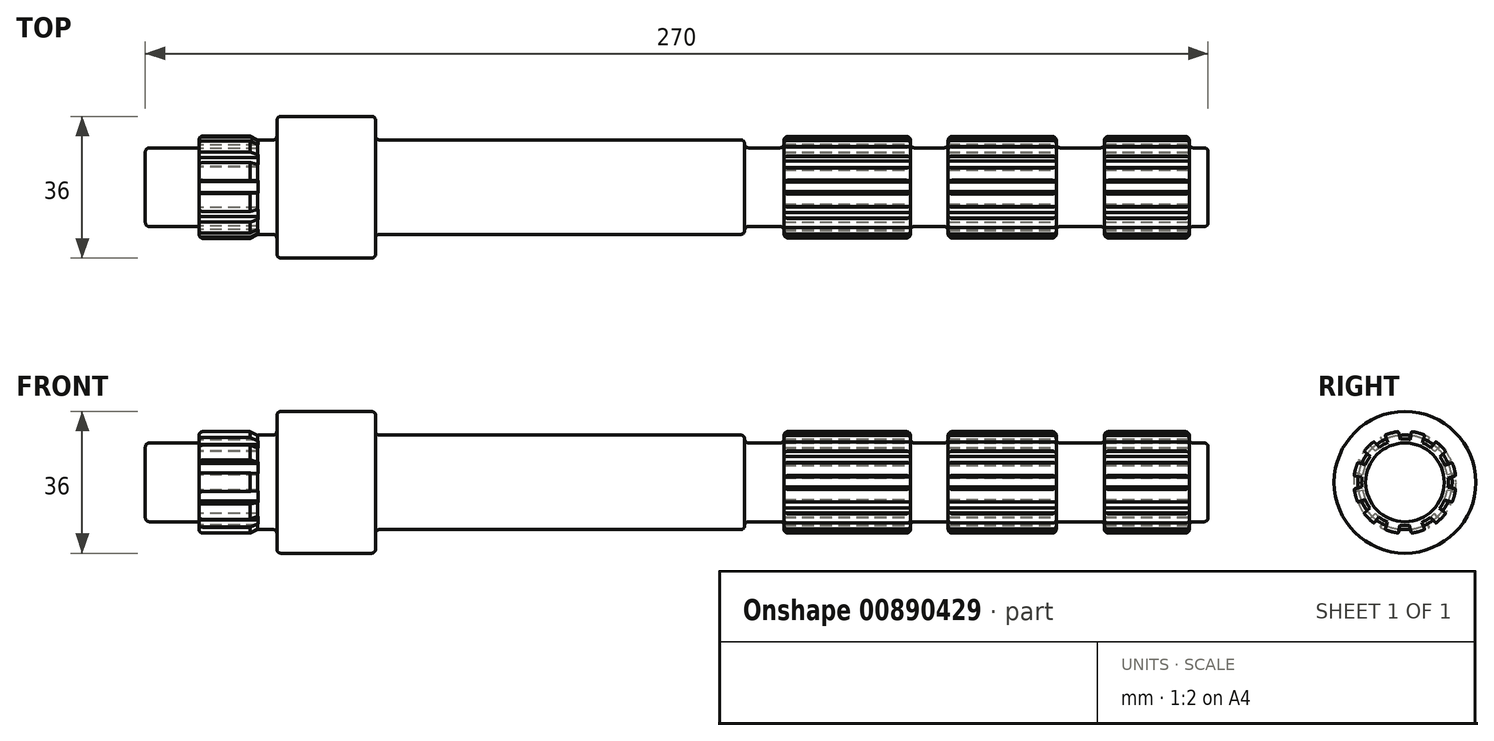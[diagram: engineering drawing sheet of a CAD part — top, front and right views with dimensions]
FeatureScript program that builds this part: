
annotation { "Feature Type Name" : "Feature", "Feature Type Description" : "" }
export const myFeature = defineFeature(function(context is Context, id is Id, definition is map)
    precondition{}
    {
        {
            var Q0;
            Q0=qCreatedBy(makeId("Front.planeOp"),FACE);
            var sketch = newSketch(context, id + "F0", { "sketchPlane" : qUnion([Q0])});
            skLineSegment(sketch, "E0", {"start": v(0, 0) * mm, "end": v(0, 9) * mm});
            skLineSegment(sketch, "E1", {"start": v(1, 10) * mm, "end": v(13.63, 10) * mm});
            skLineSegment(sketch, "E2", {"start": v(13.63, 10) * mm, "end": v(13.63, 12) * mm});
            skLineSegment(sketch, "E3", {"start": v(14.63, 13) * mm, "end": v(26.57, 13) * mm});
            skLineSegment(sketch, "E4", {"start": v(28.57, 12) * mm, "end": v(32.41, 12) * mm});
            skLineSegment(sketch, "E5", {"start": v(33.41, 13) * mm, "end": v(33.41, 17) * mm});
            skLineSegment(sketch, "E6", {"start": v(34.41, 18) * mm, "end": v(57.48, 18) * mm});
            skLineSegment(sketch, "E7", {"start": v(58.48, 17) * mm, "end": v(58.48, 13) * mm});
            skLineSegment(sketch, "E8", {"start": v(59.48, 12) * mm, "end": v(151.25, 12) * mm});
            skLineSegment(sketch, "E9", {"start": v(152.25, 11) * mm, "end": v(152.25, 11) * mm});
            skLineSegment(sketch, "E10", {"start": v(153.25, 10) * mm, "end": v(161.25, 10) * mm});
            skLineSegment(sketch, "E11", {"start": v(162.25, 11) * mm, "end": v(162.25, 12) * mm});
            skLineSegment(sketch, "E12", {"start": v(163.25, 13) * mm, "end": v(193.36, 13) * mm});
            skLineSegment(sketch, "E13", {"start": v(194.36, 12) * mm, "end": v(194.36, 11) * mm});
            skLineSegment(sketch, "E14", {"start": v(195.36, 10) * mm, "end": v(202.96, 10) * mm});
            skLineSegment(sketch, "E15", {"start": v(203.96, 11) * mm, "end": v(203.96, 12) * mm});
            skLineSegment(sketch, "E16", {"start": v(204.96, 13) * mm, "end": v(230.4, 13) * mm});
            skLineSegment(sketch, "E17", {"start": v(231.4, 12) * mm, "end": v(231.4, 11) * mm});
            skLineSegment(sketch, "E18", {"start": v(232.4, 10) * mm, "end": v(242.67, 10) * mm});
            skLineSegment(sketch, "E19", {"start": v(243.67, 11) * mm, "end": v(243.67, 12) * mm});
            skLineSegment(sketch, "E20", {"start": v(244.67, 13) * mm, "end": v(264.2, 13) * mm});
            skLineSegment(sketch, "E21", {"start": v(265.2, 12) * mm, "end": v(265.2, 11) * mm});
            skLineSegment(sketch, "E22", {"start": v(266.2, 10) * mm, "end": v(269, 10) * mm});
            skLineSegment(sketch, "E23", {"start": v(270, 9) * mm, "end": v(270, 0) * mm});
            skLineSegment(sketch, "E24", {"start": v(270, 0) * mm, "end": v(0, 0) * mm});
            skPoint(sketch, "E25.visualSharp", {"position": v(0, 10) * mm});
            skArc(sketch, "E25.filletArc", {"start": v(1, 10) * mm, "mid": v(0.3, 9.7) * mm, "end": v(0, 9) * mm});
            skPoint(sketch, "E26.visualSharp", {"position": v(13.63, 13) * mm});
            skArc(sketch, "E26.filletArc", {"start": v(14.63, 13) * mm, "mid": v(13.92, 12.7) * mm, "end": v(13.63, 12) * mm});
            skPoint(sketch, "E27.visualSharp", {"position": v(33.41, 12) * mm});
            skArc(sketch, "E27.filletArc", {"start": v(32.41, 12) * mm, "mid": v(33.12, 12.3) * mm, "end": v(33.41, 13) * mm});
            skPoint(sketch, "E28.visualSharp", {"position": v(33.41, 18) * mm});
            skArc(sketch, "E28.filletArc", {"start": v(34.41, 18) * mm, "mid": v(33.7, 17.7) * mm, "end": v(33.41, 17) * mm});
            skPoint(sketch, "E29.visualSharp", {"position": v(58.48, 18) * mm});
            skArc(sketch, "E29.filletArc", {"start": v(58.48, 17) * mm, "mid": v(58.19, 17.7) * mm, "end": v(57.48, 18) * mm});
            skPoint(sketch, "E30.visualSharp", {"position": v(58.48, 12) * mm});
            skArc(sketch, "E30.filletArc", {"start": v(58.48, 13) * mm, "mid": v(58.77, 12.3) * mm, "end": v(59.48, 12) * mm});
            skPoint(sketch, "E31.visualSharp", {"position": v(152.25, 12) * mm});
            skArc(sketch, "E31.filletArc", {"start": v(152.25, 11) * mm, "mid": v(151.96, 11.7) * mm, "end": v(151.25, 12) * mm});
            skPoint(sketch, "E32.visualSharp", {"position": v(152.25, 10) * mm});
            skArc(sketch, "E32.filletArc", {"start": v(152.25, 11) * mm, "mid": v(152.55, 10.3) * mm, "end": v(153.25, 10) * mm});
            skPoint(sketch, "E33.visualSharp", {"position": v(162.25, 10) * mm});
            skArc(sketch, "E33.filletArc", {"start": v(161.25, 10) * mm, "mid": v(161.96, 10.3) * mm, "end": v(162.25, 11) * mm});
            skPoint(sketch, "E34.visualSharp", {"position": v(162.25, 13) * mm});
            skArc(sketch, "E34.filletArc", {"start": v(163.25, 13) * mm, "mid": v(162.55, 12.7) * mm, "end": v(162.25, 12) * mm});
            skPoint(sketch, "E35.visualSharp", {"position": v(194.36, 13) * mm});
            skArc(sketch, "E35.filletArc", {"start": v(194.36, 12) * mm, "mid": v(194.07, 12.7) * mm, "end": v(193.36, 13) * mm});
            skPoint(sketch, "E36.visualSharp", {"position": v(194.36, 10) * mm});
            skArc(sketch, "E36.filletArc", {"start": v(194.36, 11) * mm, "mid": v(194.66, 10.3) * mm, "end": v(195.36, 10) * mm});
            skPoint(sketch, "E37.visualSharp", {"position": v(203.96, 10) * mm});
            skArc(sketch, "E37.filletArc", {"start": v(202.96, 10) * mm, "mid": v(203.66, 10.3) * mm, "end": v(203.96, 11) * mm});
            skPoint(sketch, "E38.visualSharp", {"position": v(203.96, 13) * mm});
            skArc(sketch, "E38.filletArc", {"start": v(204.96, 13) * mm, "mid": v(204.25, 12.7) * mm, "end": v(203.96, 12) * mm});
            skPoint(sketch, "E39.visualSharp", {"position": v(231.4, 13) * mm});
            skArc(sketch, "E39.filletArc", {"start": v(231.4, 12) * mm, "mid": v(231.12, 12.7) * mm, "end": v(230.4, 13) * mm});
            skPoint(sketch, "E40.visualSharp", {"position": v(231.4, 10) * mm});
            skArc(sketch, "E40.filletArc", {"start": v(231.4, 11) * mm, "mid": v(231.7, 10.3) * mm, "end": v(232.4, 10) * mm});
            skPoint(sketch, "E41.visualSharp", {"position": v(243.67, 10) * mm});
            skArc(sketch, "E41.filletArc", {"start": v(242.67, 10) * mm, "mid": v(243.38, 10.3) * mm, "end": v(243.67, 11) * mm});
            skPoint(sketch, "E42.visualSharp", {"position": v(243.67, 13) * mm});
            skArc(sketch, "E42.filletArc", {"start": v(244.67, 13) * mm, "mid": v(243.96, 12.7) * mm, "end": v(243.67, 12) * mm});
            skPoint(sketch, "E43.visualSharp", {"position": v(265.2, 13) * mm});
            skArc(sketch, "E43.filletArc", {"start": v(265.2, 12) * mm, "mid": v(264.9, 12.7) * mm, "end": v(264.2, 13) * mm});
            skPoint(sketch, "E44.visualSharp", {"position": v(265.2, 10) * mm});
            skArc(sketch, "E44.filletArc", {"start": v(265.2, 11) * mm, "mid": v(265.5, 10.3) * mm, "end": v(266.2, 10) * mm});
            skPoint(sketch, "E45.visualSharp", {"position": v(270, 10) * mm});
            skArc(sketch, "E45.filletArc", {"start": v(270, 9) * mm, "mid": v(269.7, 9.7) * mm, "end": v(269, 10) * mm});
            skLineSegment(sketch, "E46", {"start": v(26.57, 13) * mm, "end": v(28.57, 12) * mm});
            skSolve(sketch);
        }
        {
            var Q0;
            Q0 = qSketchRegion(id + "F0", true);
            var Q1;
            Q1=sQuery(id+"F0.wireOp",EDGE,"E24");
            revolve(context, id + "F1", {"surfaceOperationType" : NewSurfaceOperationType.NEW, "entities" : qUnion([Q0]), "axis" : qUnion([Q1]), "revolveType" : RevolveType.FULL});
        }
        {
            var Q0;
            Q0=makeQuery(id+"F1.opRevolve","SWEPT_FACE",FACE,{"disambiguationData":[OSD([sQuery(id+"F0.wireOp",EDGE,"E2")])]});
            var sketch = newSketch(context, id + "F2", { "sketchPlane" : qUnion([Q0])});
            skLineSegment(sketch, "E47", {"start": v(-1.55, 13.03) * mm, "end": v(1.45, 13.03) * mm});
            skPoint(sketch, "E48.visualSharp", {"position": v(-1.75, 13.03) * mm});
            skArc(sketch, "E48.filletArc", {"start": v(-1.55, 13.03) * mm, "mid": v(-1.7, 12.97) * mm, "end": v(-1.75, 12.83) * mm});
            skPoint(sketch, "E49.visualSharp", {"position": v(1.65, 13.03) * mm});
            skArc(sketch, "E49.filletArc", {"start": v(1.65, 12.83) * mm, "mid": v(1.6, 12.97) * mm, "end": v(1.45, 13.03) * mm});
            skLineSegment(sketch, "E50", {"start": v(-1.75, 12.83) * mm, "end": v(-1.47, 10.8) * mm});
            skLineSegment(sketch, "E51", {"start": v(1.65, 12.83) * mm, "end": v(1.4, 10.82) * mm});
            skLineSegment(sketch, "E52.1.0", {"start": v(-8.91, 9.63) * mm, "end": v(-6.49, 11.4) * mm});
            skLineSegment(sketch, "E52.1.1", {"start": v(-8.96, 9.35) * mm, "end": v(-7.54, 7.88) * mm});
            skLineSegment(sketch, "E52.1.2", {"start": v(-6.2, 11.35) * mm, "end": v(-5.23, 9.57) * mm});
            skPoint(sketch, "E52.1.3", {"position": v(-6.33, 11.51) * mm});
            skPoint(sketch, "E52.1.4", {"position": v(-9.08, 9.52) * mm});
            skArc(sketch, "E52.1.5", {"start": v(-8.91, 9.63) * mm, "mid": v(-9, 9.5) * mm, "end": v(-8.96, 9.35) * mm});
            skArc(sketch, "E52.1.6", {"start": v(-6.2, 11.35) * mm, "mid": v(-6.34, 11.43) * mm, "end": v(-6.49, 11.4) * mm});
            skLineSegment(sketch, "E52.2.0", {"start": v(-12.87, 2.55) * mm, "end": v(-11.95, 5.4) * mm});
            skLineSegment(sketch, "E52.2.1", {"start": v(-12.75, 2.3) * mm, "end": v(-10.73, 1.94) * mm});
            skLineSegment(sketch, "E52.2.2", {"start": v(-11.7, 5.53) * mm, "end": v(-9.86, 4.67) * mm});
            skPoint(sketch, "E52.2.3", {"position": v(-11.89, 5.6) * mm});
            skPoint(sketch, "E52.2.4", {"position": v(-12.94, 2.36) * mm});
            skArc(sketch, "E52.2.5", {"start": v(-12.87, 2.55) * mm, "mid": v(-12.86, 2.4) * mm, "end": v(-12.75, 2.3) * mm});
            skArc(sketch, "E52.2.6", {"start": v(-11.7, 5.53) * mm, "mid": v(-11.85, 5.52) * mm, "end": v(-11.95, 5.4) * mm});
            skLineSegment(sketch, "E52.3.0", {"start": v(-11.92, -5.5) * mm, "end": v(-12.84, -2.65) * mm});
            skLineSegment(sketch, "E52.3.1", {"start": v(-11.66, -5.63) * mm, "end": v(-9.82, -4.74) * mm});
            skLineSegment(sketch, "E52.3.2", {"start": v(-12.71, -2.4) * mm, "end": v(-10.72, -2.02) * mm});
            skPoint(sketch, "E52.3.3", {"position": v(-12.9, -2.46) * mm});
            skPoint(sketch, "E52.3.4", {"position": v(-11.85, -5.7) * mm});
            skArc(sketch, "E52.3.5", {"start": v(-11.92, -5.5) * mm, "mid": v(-11.82, -5.62) * mm, "end": v(-11.66, -5.63) * mm});
            skArc(sketch, "E52.3.6", {"start": v(-12.71, -2.4) * mm, "mid": v(-12.83, -2.5) * mm, "end": v(-12.84, -2.65) * mm});
            skLineSegment(sketch, "E52.4.0", {"start": v(-6.4, -11.45) * mm, "end": v(-8.83, -9.7) * mm});
            skLineSegment(sketch, "E52.4.1", {"start": v(-6.13, -11.41) * mm, "end": v(-5.16, -9.6) * mm});
            skLineSegment(sketch, "E52.4.2", {"start": v(-8.88, -9.41) * mm, "end": v(-7.48, -7.93) * mm});
            skPoint(sketch, "E52.4.3", {"position": v(-9, -9.57) * mm});
            skPoint(sketch, "E52.4.4", {"position": v(-6.24, -11.57) * mm});
            skArc(sketch, "E52.4.5", {"start": v(-6.4, -11.45) * mm, "mid": v(-6.26, -11.5) * mm, "end": v(-6.13, -11.41) * mm});
            skArc(sketch, "E52.4.6", {"start": v(-8.88, -9.41) * mm, "mid": v(-8.91, -9.56) * mm, "end": v(-8.83, -9.7) * mm});
            skLineSegment(sketch, "E52.5.0", {"start": v(1.55, -13.03) * mm, "end": v(-1.45, -13.03) * mm});
            skLineSegment(sketch, "E52.5.1", {"start": v(1.75, -12.83) * mm, "end": v(1.47, -10.8) * mm});
            skLineSegment(sketch, "E52.5.2", {"start": v(-1.65, -12.83) * mm, "end": v(-1.4, -10.82) * mm});
            skPoint(sketch, "E52.5.3", {"position": v(-1.65, -13.03) * mm});
            skPoint(sketch, "E52.5.4", {"position": v(1.75, -13.03) * mm});
            skArc(sketch, "E52.5.5", {"start": v(1.55, -13.03) * mm, "mid": v(1.7, -12.97) * mm, "end": v(1.75, -12.83) * mm});
            skArc(sketch, "E52.5.6", {"start": v(-1.65, -12.83) * mm, "mid": v(-1.6, -12.97) * mm, "end": v(-1.45, -13.03) * mm});
            skLineSegment(sketch, "E52.6.0", {"start": v(8.91, -9.63) * mm, "end": v(6.49, -11.4) * mm});
            skLineSegment(sketch, "E52.6.1", {"start": v(8.96, -9.35) * mm, "end": v(7.54, -7.88) * mm});
            skLineSegment(sketch, "E52.6.2", {"start": v(6.2, -11.35) * mm, "end": v(5.23, -9.57) * mm});
            skPoint(sketch, "E52.6.3", {"position": v(6.33, -11.51) * mm});
            skPoint(sketch, "E52.6.4", {"position": v(9.08, -9.52) * mm});
            skArc(sketch, "E52.6.5", {"start": v(8.91, -9.63) * mm, "mid": v(9, -9.5) * mm, "end": v(8.96, -9.35) * mm});
            skArc(sketch, "E52.6.6", {"start": v(6.2, -11.35) * mm, "mid": v(6.34, -11.43) * mm, "end": v(6.49, -11.4) * mm});
            skLineSegment(sketch, "E52.7.0", {"start": v(12.87, -2.55) * mm, "end": v(11.95, -5.4) * mm});
            skLineSegment(sketch, "E52.7.1", {"start": v(12.75, -2.3) * mm, "end": v(10.73, -1.94) * mm});
            skLineSegment(sketch, "E52.7.2", {"start": v(11.7, -5.53) * mm, "end": v(9.86, -4.67) * mm});
            skPoint(sketch, "E52.7.3", {"position": v(11.89, -5.6) * mm});
            skPoint(sketch, "E52.7.4", {"position": v(12.94, -2.36) * mm});
            skArc(sketch, "E52.7.5", {"start": v(12.87, -2.55) * mm, "mid": v(12.86, -2.4) * mm, "end": v(12.75, -2.3) * mm});
            skArc(sketch, "E52.7.6", {"start": v(11.7, -5.53) * mm, "mid": v(11.85, -5.52) * mm, "end": v(11.95, -5.4) * mm});
            skLineSegment(sketch, "E52.8.0", {"start": v(11.92, 5.5) * mm, "end": v(12.84, 2.65) * mm});
            skLineSegment(sketch, "E52.8.1", {"start": v(11.66, 5.63) * mm, "end": v(9.82, 4.74) * mm});
            skLineSegment(sketch, "E52.8.2", {"start": v(12.71, 2.4) * mm, "end": v(10.72, 2.02) * mm});
            skPoint(sketch, "E52.8.3", {"position": v(12.9, 2.46) * mm});
            skPoint(sketch, "E52.8.4", {"position": v(11.85, 5.7) * mm});
            skArc(sketch, "E52.8.5", {"start": v(11.92, 5.5) * mm, "mid": v(11.82, 5.62) * mm, "end": v(11.66, 5.63) * mm});
            skArc(sketch, "E52.8.6", {"start": v(12.71, 2.4) * mm, "mid": v(12.83, 2.5) * mm, "end": v(12.84, 2.65) * mm});
            skLineSegment(sketch, "E52.9.0", {"start": v(6.4, 11.45) * mm, "end": v(8.83, 9.7) * mm});
            skLineSegment(sketch, "E52.9.1", {"start": v(6.13, 11.41) * mm, "end": v(5.16, 9.6) * mm});
            skLineSegment(sketch, "E52.9.2", {"start": v(8.88, 9.41) * mm, "end": v(7.48, 7.93) * mm});
            skPoint(sketch, "E52.9.3", {"position": v(9, 9.57) * mm});
            skPoint(sketch, "E52.9.4", {"position": v(6.24, 11.57) * mm});
            skArc(sketch, "E52.9.5", {"start": v(6.4, 11.45) * mm, "mid": v(6.26, 11.5) * mm, "end": v(6.13, 11.41) * mm});
            skArc(sketch, "E52.9.6", {"start": v(8.88, 9.41) * mm, "mid": v(8.91, 9.56) * mm, "end": v(8.83, 9.7) * mm});
            skPoint(sketch, "E52.center", {"position": v(0, 0) * mm});
            skArc(sketch, "E53", {"start": v(-5.23, 9.57) * mm, "mid": v(-6.45, 8.8) * mm, "end": v(-7.54, 7.88) * mm});
            skArc(sketch, "E54.trimOffspring", {"start": v(1.4, 10.82) * mm, "mid": v(-0.04, 10.9) * mm, "end": v(-1.47, 10.8) * mm});
            skArc(sketch, "E55.trimOffspring", {"start": v(7.48, 7.93) * mm, "mid": v(6.38, 8.85) * mm, "end": v(5.16, 9.6) * mm});
            skArc(sketch, "E56.trimOffspring", {"start": v(10.72, 2.02) * mm, "mid": v(10.36, 3.41) * mm, "end": v(9.82, 4.74) * mm});
            skArc(sketch, "E57.trimOffspring", {"start": v(9.86, -4.67) * mm, "mid": v(10.39, -3.33) * mm, "end": v(10.73, -1.94) * mm});
            skArc(sketch, "E58.trimOffspring", {"start": v(5.23, -9.57) * mm, "mid": v(6.45, -8.8) * mm, "end": v(7.54, -7.88) * mm});
            skArc(sketch, "E59.trimOffspring", {"start": v(-1.4, -10.82) * mm, "mid": v(0.04, -10.9) * mm, "end": v(1.47, -10.8) * mm});
            skArc(sketch, "E60.trimOffspring", {"start": v(-7.48, -7.93) * mm, "mid": v(-6.38, -8.85) * mm, "end": v(-5.16, -9.6) * mm});
            skArc(sketch, "E61.trimOffspring", {"start": v(-10.72, -2.02) * mm, "mid": v(-10.36, -3.41) * mm, "end": v(-9.82, -4.74) * mm});
            skArc(sketch, "E62.trimOffspring", {"start": v(-9.86, 4.67) * mm, "mid": v(-10.39, 3.33) * mm, "end": v(-10.73, 1.94) * mm});
            skSolve(sketch);
        }
        {
            var Q0;
            Q0 = qSketchRegion(id + "F2", true);
            extrude(context, id + "F3", {"entities" : qUnion([Q0]), "operationType" : NewBodyOperationType.REMOVE, "oppositeDirection" : true, "depth" : 15 * mm, "offsetDistance" : 25 * mm});
        }
        {
            var Q0;
            Q0=makeQuery(id+"F1.opRevolve","SWEPT_FACE",FACE,{"disambiguationData":[OSD([sQuery(id+"F0.wireOp",EDGE,"E21")])]});
            var sketch = newSketch(context, id + "F4", { "sketchPlane" : qUnion([Q0])});
            skArc(sketch, "E63", {"start": v(1.32, 10.93) * mm, "mid": v(0.08, 11) * mm, "end": v(-1.17, 10.94) * mm});
            skLineSegment(sketch, "E64", {"start": v(-1.17, 10.94) * mm, "end": v(-1.62, 12.8) * mm});
            skLineSegment(sketch, "E65", {"start": v(-1.62, 12.8) * mm, "end": v(-2.02, 12.96) * mm});
            skLineSegment(sketch, "E66", {"start": v(-2.02, 12.96) * mm, "end": v(-2.58, 13.2) * mm});
            skLineSegment(sketch, "E67", {"start": v(-2.58, 13.2) * mm, "end": v(2.2, 13.2) * mm});
            skLineSegment(sketch, "E68", {"start": v(2.2, 13.2) * mm, "end": v(1.63, 12.8) * mm});
            skLineSegment(sketch, "E69", {"start": v(1.63, 12.8) * mm, "end": v(1.32, 10.92) * mm});
            skArc(sketch, "E70.1.0", {"start": v(-4.32, 10.12) * mm, "mid": v(-5.44, 9.57) * mm, "end": v(-6.48, 8.9) * mm});
            skLineSegment(sketch, "E70.1.1", {"start": v(-8.84, 10.14) * mm, "end": v(-4.69, 12.53) * mm});
            skLineSegment(sketch, "E70.1.2", {"start": v(-6.48, 8.89) * mm, "end": v(-7.8, 10.27) * mm});
            skLineSegment(sketch, "E70.1.3", {"start": v(-4.69, 12.53) * mm, "end": v(-4.99, 11.9) * mm});
            skLineSegment(sketch, "E70.1.4", {"start": v(-7.8, 10.27) * mm, "end": v(-8.23, 10.22) * mm});
            skLineSegment(sketch, "E70.1.5", {"start": v(-8.23, 10.22) * mm, "end": v(-8.84, 10.14) * mm});
            skLineSegment(sketch, "E70.1.6", {"start": v(-4.99, 11.9) * mm, "end": v(-4.32, 10.12) * mm});
            skArc(sketch, "E70.2.0", {"start": v(-8.8, 6.6) * mm, "mid": v(-9.5, 5.57) * mm, "end": v(-10.06, 4.46) * mm});
            skLineSegment(sketch, "E70.2.1", {"start": v(-12.72, 4.36) * mm, "end": v(-10.33, 8.51) * mm});
            skLineSegment(sketch, "E70.2.2", {"start": v(-10.06, 4.46) * mm, "end": v(-11.9, 5) * mm});
            skLineSegment(sketch, "E70.2.3", {"start": v(-10.33, 8.51) * mm, "end": v(-10.27, 7.81) * mm});
            skLineSegment(sketch, "E70.2.4", {"start": v(-11.9, 5) * mm, "end": v(-12.24, 4.73) * mm});
            skLineSegment(sketch, "E70.2.5", {"start": v(-12.24, 4.73) * mm, "end": v(-12.72, 4.36) * mm});
            skLineSegment(sketch, "E70.2.6", {"start": v(-10.27, 7.81) * mm, "end": v(-8.8, 6.6) * mm});
            skArc(sketch, "E70.3.0", {"start": v(-10.93, 1.32) * mm, "mid": v(-11, 0.08) * mm, "end": v(-10.94, -1.17) * mm});
            skLineSegment(sketch, "E70.3.1", {"start": v(-13.2, -2.58) * mm, "end": v(-13.2, 2.2) * mm});
            skLineSegment(sketch, "E70.3.2", {"start": v(-10.94, -1.17) * mm, "end": v(-12.8, -1.62) * mm});
            skLineSegment(sketch, "E70.3.3", {"start": v(-13.2, 2.2) * mm, "end": v(-12.8, 1.63) * mm});
            skLineSegment(sketch, "E70.3.4", {"start": v(-12.8, -1.62) * mm, "end": v(-12.96, -2.02) * mm});
            skLineSegment(sketch, "E70.3.5", {"start": v(-12.96, -2.02) * mm, "end": v(-13.2, -2.58) * mm});
            skLineSegment(sketch, "E70.3.6", {"start": v(-12.8, 1.63) * mm, "end": v(-10.92, 1.32) * mm});
            skArc(sketch, "E70.4.0", {"start": v(-10.12, -4.32) * mm, "mid": v(-9.57, -5.44) * mm, "end": v(-8.9, -6.48) * mm});
            skLineSegment(sketch, "E70.4.1", {"start": v(-10.14, -8.84) * mm, "end": v(-12.53, -4.69) * mm});
            skLineSegment(sketch, "E70.4.2", {"start": v(-8.89, -6.48) * mm, "end": v(-10.27, -7.8) * mm});
            skLineSegment(sketch, "E70.4.3", {"start": v(-12.53, -4.69) * mm, "end": v(-11.9, -4.99) * mm});
            skLineSegment(sketch, "E70.4.4", {"start": v(-10.27, -7.8) * mm, "end": v(-10.22, -8.23) * mm});
            skLineSegment(sketch, "E70.4.5", {"start": v(-10.22, -8.23) * mm, "end": v(-10.14, -8.84) * mm});
            skLineSegment(sketch, "E70.4.6", {"start": v(-11.9, -4.99) * mm, "end": v(-10.12, -4.32) * mm});
            skArc(sketch, "E70.5.0", {"start": v(-6.6, -8.8) * mm, "mid": v(-5.57, -9.5) * mm, "end": v(-4.46, -10.06) * mm});
            skLineSegment(sketch, "E70.5.1", {"start": v(-4.36, -12.72) * mm, "end": v(-8.51, -10.33) * mm});
            skLineSegment(sketch, "E70.5.2", {"start": v(-4.46, -10.06) * mm, "end": v(-5, -11.9) * mm});
            skLineSegment(sketch, "E70.5.3", {"start": v(-8.51, -10.33) * mm, "end": v(-7.81, -10.27) * mm});
            skLineSegment(sketch, "E70.5.4", {"start": v(-5, -11.9) * mm, "end": v(-4.73, -12.24) * mm});
            skLineSegment(sketch, "E70.5.5", {"start": v(-4.73, -12.24) * mm, "end": v(-4.36, -12.72) * mm});
            skLineSegment(sketch, "E70.5.6", {"start": v(-7.81, -10.27) * mm, "end": v(-6.6, -8.8) * mm});
            skArc(sketch, "E70.6.0", {"start": v(-1.32, -10.93) * mm, "mid": v(-0.08, -11) * mm, "end": v(1.17, -10.94) * mm});
            skLineSegment(sketch, "E70.6.1", {"start": v(2.58, -13.2) * mm, "end": v(-2.2, -13.2) * mm});
            skLineSegment(sketch, "E70.6.2", {"start": v(1.17, -10.94) * mm, "end": v(1.62, -12.8) * mm});
            skLineSegment(sketch, "E70.6.3", {"start": v(-2.2, -13.2) * mm, "end": v(-1.63, -12.8) * mm});
            skLineSegment(sketch, "E70.6.4", {"start": v(1.62, -12.8) * mm, "end": v(2.02, -12.96) * mm});
            skLineSegment(sketch, "E70.6.5", {"start": v(2.02, -12.96) * mm, "end": v(2.58, -13.2) * mm});
            skLineSegment(sketch, "E70.6.6", {"start": v(-1.63, -12.8) * mm, "end": v(-1.32, -10.92) * mm});
            skArc(sketch, "E70.7.0", {"start": v(4.32, -10.12) * mm, "mid": v(5.44, -9.57) * mm, "end": v(6.48, -8.9) * mm});
            skLineSegment(sketch, "E70.7.1", {"start": v(8.84, -10.14) * mm, "end": v(4.69, -12.53) * mm});
            skLineSegment(sketch, "E70.7.2", {"start": v(6.48, -8.89) * mm, "end": v(7.8, -10.27) * mm});
            skLineSegment(sketch, "E70.7.3", {"start": v(4.69, -12.53) * mm, "end": v(4.99, -11.9) * mm});
            skLineSegment(sketch, "E70.7.4", {"start": v(7.8, -10.27) * mm, "end": v(8.23, -10.22) * mm});
            skLineSegment(sketch, "E70.7.5", {"start": v(8.23, -10.22) * mm, "end": v(8.84, -10.14) * mm});
            skLineSegment(sketch, "E70.7.6", {"start": v(4.99, -11.9) * mm, "end": v(4.32, -10.12) * mm});
            skArc(sketch, "E70.8.0", {"start": v(8.8, -6.6) * mm, "mid": v(9.5, -5.57) * mm, "end": v(10.06, -4.46) * mm});
            skLineSegment(sketch, "E70.8.1", {"start": v(12.72, -4.36) * mm, "end": v(10.33, -8.51) * mm});
            skLineSegment(sketch, "E70.8.2", {"start": v(10.06, -4.46) * mm, "end": v(11.9, -5) * mm});
            skLineSegment(sketch, "E70.8.3", {"start": v(10.33, -8.51) * mm, "end": v(10.27, -7.81) * mm});
            skLineSegment(sketch, "E70.8.4", {"start": v(11.9, -5) * mm, "end": v(12.24, -4.73) * mm});
            skLineSegment(sketch, "E70.8.5", {"start": v(12.24, -4.73) * mm, "end": v(12.72, -4.36) * mm});
            skLineSegment(sketch, "E70.8.6", {"start": v(10.27, -7.81) * mm, "end": v(8.8, -6.6) * mm});
            skArc(sketch, "E70.9.0", {"start": v(10.93, -1.32) * mm, "mid": v(11, -0.08) * mm, "end": v(10.94, 1.17) * mm});
            skLineSegment(sketch, "E70.9.1", {"start": v(13.2, 2.58) * mm, "end": v(13.2, -2.2) * mm});
            skLineSegment(sketch, "E70.9.2", {"start": v(10.94, 1.17) * mm, "end": v(12.8, 1.62) * mm});
            skLineSegment(sketch, "E70.9.3", {"start": v(13.2, -2.2) * mm, "end": v(12.8, -1.63) * mm});
            skLineSegment(sketch, "E70.9.4", {"start": v(12.8, 1.62) * mm, "end": v(12.96, 2.02) * mm});
            skLineSegment(sketch, "E70.9.5", {"start": v(12.96, 2.02) * mm, "end": v(13.2, 2.58) * mm});
            skLineSegment(sketch, "E70.9.6", {"start": v(12.8, -1.63) * mm, "end": v(10.92, -1.32) * mm});
            skArc(sketch, "E70.10.0", {"start": v(10.12, 4.32) * mm, "mid": v(9.57, 5.44) * mm, "end": v(8.9, 6.48) * mm});
            skLineSegment(sketch, "E70.10.1", {"start": v(10.14, 8.84) * mm, "end": v(12.53, 4.69) * mm});
            skLineSegment(sketch, "E70.10.2", {"start": v(8.89, 6.48) * mm, "end": v(10.27, 7.8) * mm});
            skLineSegment(sketch, "E70.10.3", {"start": v(12.53, 4.69) * mm, "end": v(11.9, 4.99) * mm});
            skLineSegment(sketch, "E70.10.4", {"start": v(10.27, 7.8) * mm, "end": v(10.22, 8.23) * mm});
            skLineSegment(sketch, "E70.10.5", {"start": v(10.22, 8.23) * mm, "end": v(10.14, 8.84) * mm});
            skLineSegment(sketch, "E70.10.6", {"start": v(11.9, 4.99) * mm, "end": v(10.12, 4.32) * mm});
            skArc(sketch, "E70.11.0", {"start": v(6.6, 8.8) * mm, "mid": v(5.57, 9.5) * mm, "end": v(4.46, 10.06) * mm});
            skLineSegment(sketch, "E70.11.1", {"start": v(4.36, 12.72) * mm, "end": v(8.51, 10.33) * mm});
            skLineSegment(sketch, "E70.11.2", {"start": v(4.46, 10.06) * mm, "end": v(5, 11.9) * mm});
            skLineSegment(sketch, "E70.11.3", {"start": v(8.51, 10.33) * mm, "end": v(7.81, 10.27) * mm});
            skLineSegment(sketch, "E70.11.4", {"start": v(5, 11.9) * mm, "end": v(4.73, 12.24) * mm});
            skLineSegment(sketch, "E70.11.5", {"start": v(4.73, 12.24) * mm, "end": v(4.36, 12.72) * mm});
            skLineSegment(sketch, "E70.11.6", {"start": v(7.81, 10.27) * mm, "end": v(6.6, 8.8) * mm});
            skSolve(sketch);
        }
        {
            var Q0;
            Q0 = qSketchRegion(id + "F4", true);
            extrude(context, id + "F5", {"entities" : qUnion([Q0]), "operationType" : NewBodyOperationType.REMOVE, "oppositeDirection" : true, "depth" : 110 * mm, "offsetDistance" : 25 * mm});
        }
    });
